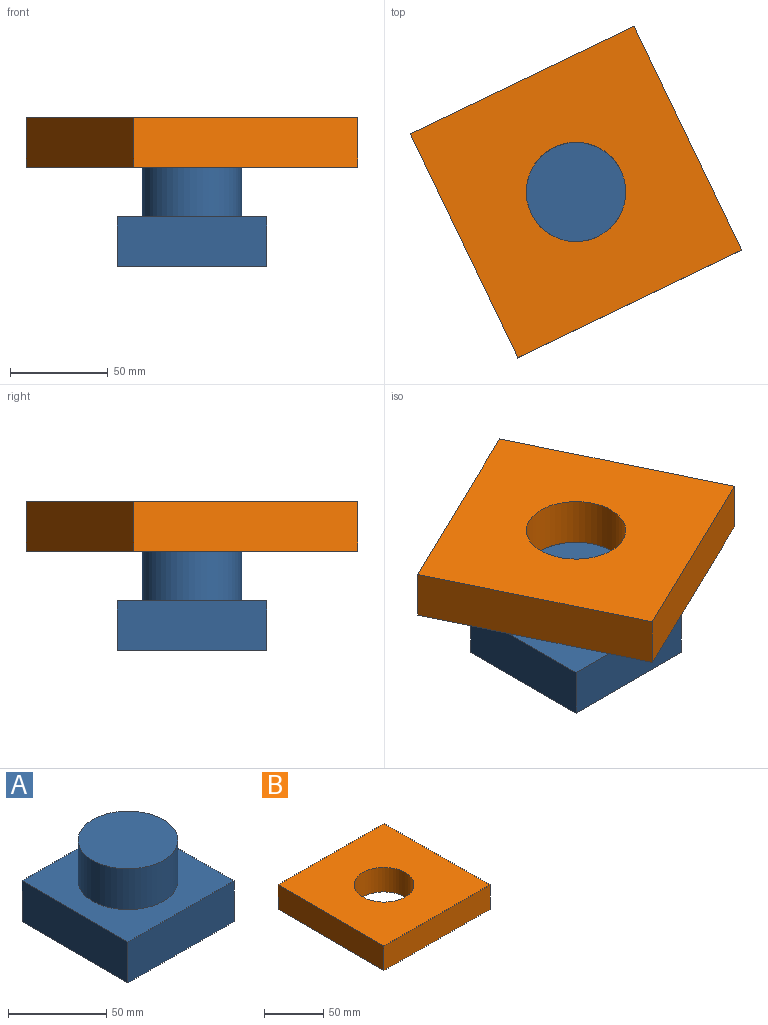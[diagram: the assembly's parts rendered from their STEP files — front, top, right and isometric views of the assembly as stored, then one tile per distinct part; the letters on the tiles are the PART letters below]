
ASSEMBLY  parts=2 mates=1
PART A: 8 faces, bbox 76.2x76.2x50.8 mm
  f0: plane 76.2x25.4mm, normal (1,0,0), area 1935.5mm2, adj f1,f3,f4,f5
  f1: plane 76.2x25.4mm, normal (0,1,0), area 1935.5mm2, adj f0,f2,f4,f5
  f2: plane 76.2x25.4mm, normal (-1,0,0), area 1935.5mm2, adj f1,f3,f4,f5
  f3: plane 76.2x25.4mm, normal (0,-1,0), area 1935.5mm2, adj f0,f2,f4,f5
  f4: plane 76.2x76.2mm, normal (0,0,1), area 3779.6mm2, adj f0,f1,f2,f3,f6
  f5: plane 76.2x76.2mm, normal (0,0,-1), area 5806.4mm2, adj f0,f1,f2,f3
  f6: cylinder r=25.4mm len=50.8mm, axis (0,0,-1), area 4053.7mm2, adj f4,f7
  f7: plane 50.8x50.8mm, normal (0,0,1), area 2026.8mm2, adj f6
PART B: 7 faces, bbox 127x127x25.4 mm
  f0: plane 127x25.4mm, normal (1,0,0), area 3225.8mm2, adj f1,f3,f5,f6
  f1: plane 127x25.4mm, normal (0,1,0), area 3225.8mm2, adj f0,f2,f5,f6
  f2: plane 127x25.4mm, normal (-1,0,0), area 3225.8mm2, adj f1,f3,f5,f6
  f3: plane 127x25.4mm, normal (0,-1,0), area 3225.8mm2, adj f0,f2,f5,f6
  f4: cylinder r=25.4mm len=50.8mm, axis (0,0,-1), area 4053.7mm2, adj f5,f6
  f5: plane 127x127mm, normal (0,0,1), area 14102.2mm2, adj f0,f1,f2,f3,f4
  f6: plane 127x127mm, normal (0,0,-1), area 14102.2mm2, adj f0,f1,f2,f3,f4
PLACE A t=(-32.51,-5.38,-5.31)mm fixed
PLACE B rot(axis=(0,0,-1),64.3deg) t=(-32.51,-5.38,45.49)mm
MATE revolute B.f4 <-> A.f6  axis (0,0,-1) through (-32.51,-5.38,45.49)mm
